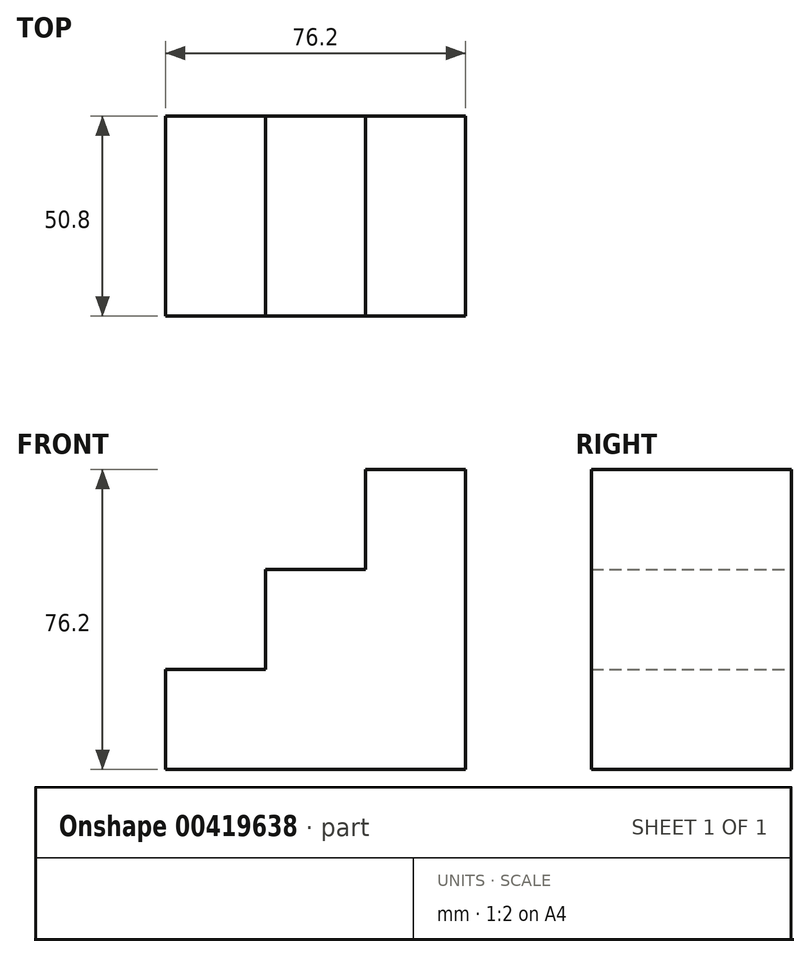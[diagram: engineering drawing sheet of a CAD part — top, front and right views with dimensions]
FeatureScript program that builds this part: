
annotation { "Feature Type Name" : "Feature", "Feature Type Description" : "" }
export const myFeature = defineFeature(function(context is Context, id is Id, definition is map)
    precondition{}
    {
        {
            var Q0;
            Q0=qCreatedBy(makeId("Front.planeOp"),FACE);
            var sketch = newSketch(context, id + "F0", { "sketchPlane" : qUnion([Q0])});
            skLineSegment(sketch, "E0", {"start": v(0, 0) * mm, "end": v(76.2, 0) * mm});
            skLineSegment(sketch, "E1", {"start": v(76.2, 0) * mm, "end": v(76.2, 76.2) * mm});
            skLineSegment(sketch, "E2", {"start": v(76.2, 76.2) * mm, "end": v(50.8, 76.2) * mm});
            skLineSegment(sketch, "E3", {"start": v(50.8, 76.2) * mm, "end": v(50.8, 50.8) * mm});
            skLineSegment(sketch, "E4", {"start": v(50.8, 50.8) * mm, "end": v(25.4, 50.8) * mm});
            skLineSegment(sketch, "E5", {"start": v(25.4, 50.8) * mm, "end": v(25.4, 25.4) * mm});
            skLineSegment(sketch, "E6", {"start": v(25.4, 25.4) * mm, "end": v(0, 25.4) * mm});
            skLineSegment(sketch, "E7", {"start": v(0, 0) * mm, "end": v(0, 25.4) * mm});
            skSolve(sketch);
        }
        {
            var Q0;
            Q0 = qSketchRegion(id + "F0", true);
            extrude(context, id + "F1", {"entities" : qUnion([Q0]), "depth" : 50.8 * mm});
        }
    });
